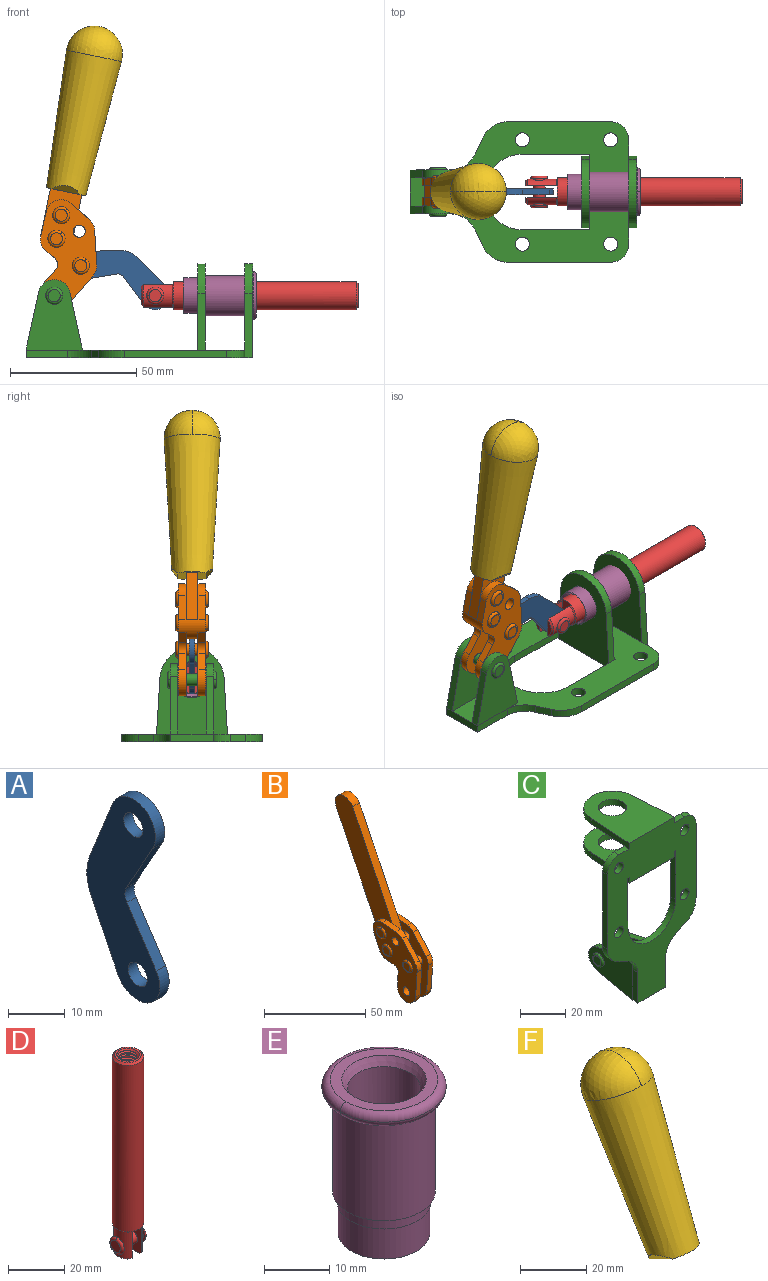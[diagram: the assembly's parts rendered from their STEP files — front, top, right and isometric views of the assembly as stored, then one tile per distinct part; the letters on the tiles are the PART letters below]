
ASSEMBLY  parts=6 mates=6
PART A: 12 faces, bbox 2.3x18.2x42.8 mm
  f0: cylinder r=2.4mm len=4.8mm, axis (1,0,0), area 34.9mm2, adj f4,f11
  f1: cylinder r=10.41mm len=8.47mm, axis (1,0,0), area 20.2mm2, adj f4,f9,f10,f11
  f2: cylinder r=3.05mm len=3.16mm, axis (1,0,0), area 7.7mm2, adj f4,f6,f7,f11
  f3: cylinder r=2.4mm len=4.8mm, axis (1,0,0), area 34.9mm2, adj f4,f11
  f4: plane 42.81x18.23mm, normal (-1,0,0), area 414.1mm2, adj f0,f1,f2,f3,f5,f6,f7,f8
  f5: cylinder r=5.54mm len=10.67mm, axis (1,0,0), area 41.8mm2, adj f4,f6,f10,f11
  f6: plane 11.66x6.53mm, normal (0,-0.87,-0.49), area 30.9mm2, adj f2,f4,f5,f11
  f7: plane 11.17x7.33mm, normal (0,-0.84,0.55), area 30.9mm2, adj f2,f4,f8,f11
  f8: cylinder r=5.54mm len=10.51mm, axis (1,0,0), area 41.8mm2, adj f4,f7,f9,f11
  f9: plane 13.67x6.67mm, normal (0,0.9,-0.44), area 35.1mm2, adj f1,f4,f8,f11
  f10: plane 14.1x5.7mm, normal (0,0.93,0.37), area 35.1mm2, adj f1,f4,f5,f11
  f11: plane 42.81x18.23mm, normal (1,0,0), area 414.1mm2, adj f0,f1,f2,f3,f5,f6,f7,f8
PART B: 59 faces, bbox 12.9x60.2x99.6 mm
  f0: torus R=2.39mm, axis (-1,0,0), area 14.9mm2, adj f20,f43,f51
  f1: torus R=2.39mm, axis (-1,0,0), area 14.9mm2, adj f19,f42,f51
  f2: torus R=2.39mm, axis (-1,0,0), area 14.9mm2, adj f18,f35,f51
  f3: torus R=2.39mm, axis (-1,0,0), area 14.9mm2, adj f14,f17,f23
  f4: torus R=2.39mm, axis (-1,0,0), area 14.9mm2, adj f13,f16,f23
  f5: torus R=2.39mm, axis (-1,0,0), area 14.9mm2, adj f12,f15,f23
  f6: cylinder r=2.39mm len=4.78mm, axis (1,0,0), area 46.5mm2, adj f48,f50,f51
  f7: cylinder r=2.39mm len=4.78mm, axis (1,0,0), area 46.5mm2, adj f50,f51
  f8: cylinder r=6.35mm len=12.68mm, axis (1,0,0), area 61.8mm2, adj f38,f39,f50,f51
  f9: cylinder r=2.39mm len=4.78mm, axis (-1,0,0), area 70.5mm2, adj f46,f50
  f10: cylinder r=2.39mm len=4.78mm, axis (-1,0,0), area 46.5mm2, adj f23,f45,f46
  f11: cylinder r=2.39mm len=4.78mm, axis (-1,0,0), area 46.5mm2, adj f23,f46
  f12: plane 4.78x4.78mm, normal (1,0,0), area 17.9mm2, adj f5,f15
  f13: plane 4.78x4.78mm, normal (1,0,0), area 17.9mm2, adj f4,f16
  f14: plane 4.78x4.78mm, normal (1,0,0), area 17.9mm2, adj f3,f17
  f15: torus R=2.39mm, axis (-1,0,0), area 14.9mm2, adj f5,f12,f23
  f16: torus R=2.39mm, axis (-1,0,0), area 14.9mm2, adj f4,f13,f23
  f17: torus R=2.39mm, axis (-1,0,0), area 14.9mm2, adj f3,f14,f23
  f18: plane 4.78x4.78mm, normal (-1,0,0), area 17.9mm2, adj f2,f35
  f19: plane 4.78x4.78mm, normal (-1,0,0), area 17.9mm2, adj f1,f42
  f20: plane 4.78x4.78mm, normal (-1,0,0), area 17.9mm2, adj f0,f43
  f21: plane 2.26x0.2mm, normal (1,0,0), area 0.2mm2, adj f31,f44
  f22: plane 2.26x0.2mm, normal (-1,0,0), area 0.2mm2, adj f41,f44
  f23: plane 39.37x30.77mm, normal (1,0,0), area 565.5mm2, adj f3,f4,f5,f10,f11,f15,f16,f17
  f24: cylinder r=6.1mm len=4.15mm, axis (-1,0,0), area 14.7mm2, adj f23,f25,f32,f46
  f25: plane 10.25x9.01mm, normal (0,-0.75,0.66), area 42.3mm2, adj f23,f24,f26,f46
  f26: cylinder r=6.35mm len=4.64mm, axis (-1,0,0), area 15.6mm2, adj f23,f25,f27,f46
  f27: plane 15.84x3.1mm, normal (0,-1,-0.07), area 49.2mm2, adj f23,f26,f28,f46
  f28: cylinder r=6.35mm len=12.68mm, axis (-1,0,0), area 61.8mm2, adj f23,f27,f29,f46
  f29: plane 8.11x3.1mm, normal (0,1,0.07), area 25.2mm2, adj f23,f28,f30,f46
  f30: cylinder r=3.05mm len=3.25mm, axis (-1,0,0), area 14.8mm2, adj f23,f29,f31,f46
  f31: plane 5.99x3.1mm, normal (0,0.07,-1), area 18.6mm2, adj f21,f23,f30,f44,f46
  f32: plane 9.5x3.1mm, normal (0,-0.07,1), area 29.5mm2, adj f23,f24,f33,f46,f47
  f33: cylinder r=6.1mm len=8.63mm, axis (-1,0,0), area 39.1mm2, adj f23,f32,f34,f47
  f34: plane 8.65x3.96mm, normal (0,0.91,-0.42), area 29.5mm2, adj f23,f33,f44,f47
  f35: torus R=2.39mm, axis (-1,0,0), area 14.9mm2, adj f2,f18,f51
  f36: plane 10.25x9.01mm, normal (0,-0.75,0.66), area 42.3mm2, adj f37,f49,f50,f51
  f37: cylinder r=6.35mm len=4.64mm, axis (1,0,0), area 15.6mm2, adj f36,f38,f50,f51
  f38: plane 15.84x3.1mm, normal (0,-1,-0.07), area 49.2mm2, adj f8,f37,f50,f51
  f39: plane 8.11x3.1mm, normal (0,1,0.07), area 25.2mm2, adj f8,f40,f50,f51
  f40: cylinder r=3.05mm len=3.25mm, axis (1,0,0), area 14.8mm2, adj f39,f41,f50,f51
  f41: plane 5.99x3.1mm, normal (0,0.07,-1), area 18.6mm2, adj f22,f40,f44,f50,f51
  f42: torus R=2.39mm, axis (-1,0,0), area 14.9mm2, adj f1,f19,f51
  f43: torus R=2.39mm, axis (-1,0,0), area 14.9mm2, adj f0,f20,f51
  f44: cylinder r=6.35mm len=12.12mm, axis (-1,0,0), area 128.9mm2, adj f21,f22,f23,f31,f34,f41,f46,f47
  f45: plane 2.65x1.35mm, normal (1,0,0), area 1mm2, adj f10,f55
  f46: plane 39.08x20.42mm, normal (-1,0,0), area 412.5mm2, adj f9,f10,f11,f24,f25,f26,f27,f28
  f47: plane 77.62x39.82mm, normal (1,0,0), area 850mm2, adj f32,f33,f34,f44,f53,f54,f55
  f48: plane 2.65x1.35mm, normal (-1,0,0), area 1mm2, adj f6,f55
  f49: cylinder r=6.1mm len=4.15mm, axis (1,0,0), area 14.7mm2, adj f36,f50,f51,f56
  f50: plane 39.08x20.42mm, normal (1,0,0), area 412.5mm2, adj f6,f7,f8,f9,f36,f37,f38,f39
  f51: plane 39.37x30.77mm, normal (-1,0,0), area 565.5mm2, adj f0,f1,f2,f6,f7,f8,f35,f36
  f52: plane 8.65x3.96mm, normal (0,0.91,-0.42), area 29.5mm2, adj f44,f51,f57,f58
  f53: plane 68.49x33.4mm, normal (0,0.9,-0.44), area 358.1mm2, adj f44,f47,f54,f58
  f54: cylinder r=6.35mm len=12.06mm, axis (1,0,0), area 93.7mm2, adj f47,f53,f55,f58
  f55: plane 68.49x33.4mm, normal (0,-0.9,0.44), area 358.1mm2, adj f44,f45,f46,f47,f48,f50,f54,f58
  f56: plane 9.5x3.1mm, normal (0,-0.07,1), area 29.5mm2, adj f49,f50,f51,f57,f58
  f57: cylinder r=6.1mm len=8.63mm, axis (1,0,0), area 39.1mm2, adj f51,f52,f56,f58
  f58: plane 77.62x39.82mm, normal (-1,0,0), area 850mm2, adj f44,f52,f53,f54,f55,f56,f57
PART C: 55 faces, bbox 55.7x37.4x89.8 mm
  f0: torus R=2.41mm, axis (-1,0,0), area 15mm2, adj f11,f15,f25
  f1: torus R=2.41mm, axis (-1,0,0), area 15mm2, adj f10,f12,f22
  f2: cylinder r=2.78mm len=5.56mm, axis (0,-1,0), area 54.2mm2, adj f30,f54
  f3: cylinder r=14.99mm len=29.97mm, axis (0,-1,0), area 145.9mm2, adj f30,f49,f53,f54
  f4: cylinder r=2.78mm len=5.56mm, axis (0,-1,0), area 54.2mm2, adj f30,f54
  f5: cylinder r=2.78mm len=5.56mm, axis (0,-1,0), area 54.2mm2, adj f30,f54
  f6: cylinder r=2.78mm len=5.56mm, axis (0,-1,0), area 54.2mm2, adj f30,f54
  f7: cylinder r=6.35mm len=12.7mm, axis (0,0,1), area 123.6mm2, adj f27,f51
  f8: cylinder r=6.35mm len=12.7mm, axis (0,0,-1), area 124.7mm2, adj f21,f35
  f9: cylinder r=2.41mm len=11.18mm, axis (-1,0,0), area 169.4mm2, adj f16,f19
  f10: plane 4.83x4.83mm, normal (1,0,0), area 18.3mm2, adj f1,f12
  f11: plane 4.83x4.83mm, normal (-1,0,0), area 18.3mm2, adj f0,f15
  f12: torus R=2.41mm, axis (-1,0,0), area 15mm2, adj f1,f10,f22
  f13: cylinder r=6.35mm len=12.41mm, axis (1,0,0), area 53.4mm2, adj f18,f19,f22,f23
  f14: cylinder r=6.35mm len=12.41mm, axis (-1,0,0), area 53.4mm2, adj f16,f17,f24,f25
  f15: torus R=2.41mm, axis (-1,0,0), area 15mm2, adj f0,f11,f25
  f16: plane 27.86x22.35mm, normal (1,0,0), area 425.4mm2, adj f9,f14,f17,f24,f30
  f17: plane 22.86x4.97mm, normal (0,0.21,0.98), area 72.5mm2, adj f14,f16,f25,f30
  f18: plane 22.86x4.97mm, normal (0,0.21,0.98), area 72.5mm2, adj f13,f19,f22,f30
  f19: plane 27.86x22.35mm, normal (-1,0,0), area 425.4mm2, adj f9,f13,f18,f23,f30
  f20: cylinder r=12.7mm len=25.35mm, axis (0,0,-1), area 119.8mm2, adj f21,f34,f35,f36
  f21: plane 34.21x28.07mm, normal (0,0,-1), area 702.4mm2, adj f8,f20,f30,f34,f36
  f22: plane 27.96x22.45mm, normal (1,0,0), area 407.2mm2, adj f1,f12,f13,f18,f23,f30,f42,f43
  f23: plane 22.86x4.97mm, normal (0,0.21,-0.98), area 72.5mm2, adj f13,f19,f22,f44
  f24: plane 22.86x4.97mm, normal (0,0.21,-0.98), area 72.5mm2, adj f14,f16,f25,f44
  f25: plane 27.86x22.35mm, normal (-1,0,0), area 407.1mm2, adj f0,f14,f15,f17,f24,f30,f45,f46
  f26: plane 3.1x0.95mm, normal (0,0,-1), area 2.7mm2, adj f30,f49,f50,f54
  f27: plane 34.21x28.07mm, normal (0,0,1), area 702.4mm2, adj f7,f28,f30,f50,f52
  f28: cylinder r=12.7mm len=25.35mm, axis (0,0,1), area 118.8mm2, adj f27,f50,f51,f52
  f29: plane 3.1x0.95mm, normal (0,0,-1), area 2.7mm2, adj f30,f52,f53,f54
  f30: plane 86.54x55.63mm, normal (0,1,0), area 2362.9mm2, adj f2,f3,f4,f5,f6,f16,f17,f18
  f31: plane 40.56x3.1mm, normal (-1,0,0), area 125.7mm2, adj f30,f32,f48,f54
  f32: cylinder r=7.11mm len=7.11mm, axis (0,-1,0), area 34.6mm2, adj f30,f31,f33,f54
  f33: plane 6.67x3.1mm, normal (0,0,1), area 20.4mm2, adj f30,f32,f34,f54
  f34: plane 25.39x3.13mm, normal (-1,0.06,0), area 79.5mm2, adj f20,f21,f33,f35,f54
  f35: plane 37.31x28.45mm, normal (0,0,1), area 789.9mm2, adj f8,f20,f34,f36,f54
  f36: plane 25.39x3.13mm, normal (1,0.06,0), area 79.5mm2, adj f20,f21,f35,f37,f54
  f37: plane 6.67x3.1mm, normal (0,0,1), area 20.4mm2, adj f30,f36,f38,f54
  f38: cylinder r=7.11mm len=7.11mm, axis (0,-1,0), area 34.6mm2, adj f30,f37,f39,f54
  f39: plane 40.56x3.1mm, normal (1,0,0), area 125.7mm2, adj f30,f38,f40,f54
  f40: cylinder r=11.18mm len=10.16mm, axis (0,-1,0), area 39.5mm2, adj f30,f39,f41,f54
  f41: plane 6.09x3.1mm, normal (0.42,0,-0.91), area 20.8mm2, adj f30,f40,f42,f54
  f42: cylinder r=11.18mm len=9.41mm, axis (0,-1,0), area 37.2mm2, adj f22,f30,f41,f43,f54
  f43: plane 16.5x3.1mm, normal (1,0,0), area 51.1mm2, adj f22,f42,f44,f54
  f44: plane 17.37x3.1mm, normal (0,0,-1), area 53.8mm2, adj f23,f24,f30,f43,f45,f54
  f45: plane 16.5x3.1mm, normal (-1,0,0), area 51.1mm2, adj f25,f44,f46,f54
  f46: cylinder r=11.18mm len=9.41mm, axis (0,-1,0), area 37.2mm2, adj f25,f30,f45,f47,f54
  f47: plane 6.09x3.1mm, normal (-0.42,0,-0.91), area 20.8mm2, adj f30,f46,f48,f54
  f48: cylinder r=11.18mm len=10.16mm, axis (0,-1,0), area 39.5mm2, adj f30,f31,f47,f54
  f49: plane 26.54x3.1mm, normal (-1,0,0), area 82.3mm2, adj f3,f26,f30,f54
  f50: plane 25.39x3.1mm, normal (1,0.06,0), area 78.8mm2, adj f26,f27,f28,f51,f54
  f51: plane 37.31x28.45mm, normal (0,0,-1), area 789.9mm2, adj f7,f28,f50,f52,f54
  f52: plane 25.39x3.1mm, normal (-1,0.06,0), area 78.8mm2, adj f27,f28,f29,f51,f54
  f53: plane 26.54x3.1mm, normal (1,0,0), area 82.3mm2, adj f3,f29,f30,f54
  f54: plane 89.66x55.63mm, normal (0,-1,0), area 2678.5mm2, adj f2,f3,f4,f5,f6,f26,f29,f31
PART D: 48 faces, bbox 12.6x11.1x86.1 mm
  f0: torus R=2.41mm, axis (-1,0,0), area 15mm2, adj f30,f32,f34
  f1: torus R=2.41mm, axis (-1,0,0), area 15mm2, adj f29,f31,f33
  f2: cylinder r=5.54mm len=72.39mm, axis (0,0,1), area 2518.5mm2, adj f3,f4,f42,f43
  f3: cone r=5.54mm half-angle=45deg, axis (0,0,1), area 7.6mm2, adj f2,f5,f41
  f4: cone r=5.54mm half-angle=45deg, axis (0,0,-1), area 34.9mm2, adj f2,f39
  f5: cylinder r=5.08mm len=11.48mm, axis (0,0,1), area 108.3mm2, adj f3,f7,f8,f41
  f6: cylinder r=2.41mm len=4.83mm, axis (-1,0,0), area 71.2mm2, adj f40,f41
  f7: cylinder r=2.41mm len=4.83mm, axis (-1,0,0), area 7.6mm2, adj f5,f34
  f8: cone r=5.08mm half-angle=45deg, axis (0,0,1), area 10.6mm2, adj f5,f37,f41
  f9: cone r=3.98mm half-angle=45deg, axis (0,0,1), area 17.6mm2, adj f27,f39,f45,f46,f47
  f10: cylinder r=2.41mm len=4.83mm, axis (-1,0,0), area 7.6mm2, adj f33,f38
  f11: cylinder r=3.2mm len=6.4mm, axis (0,0,1), area 78.4mm2, adj f12,f28,f44,f45,f47
  f12: cylinder r=3.2mm len=6.4mm, axis (0,0,1), area 10.5mm2, adj f11,f13,f45,f47
  f13: cylinder r=3.2mm len=6.4mm, axis (0,0,1), area 10.5mm2, adj f12,f14,f45,f47
  f14: cylinder r=3.2mm len=6.4mm, axis (0,0,1), area 10.5mm2, adj f13,f15,f45,f47
  f15: cylinder r=3.2mm len=6.4mm, axis (0,0,1), area 10.5mm2, adj f14,f16,f45,f47
  f16: cylinder r=3.2mm len=6.4mm, axis (0,0,1), area 10.5mm2, adj f15,f17,f45,f47
  f17: cylinder r=3.2mm len=6.4mm, axis (0,0,1), area 10.5mm2, adj f16,f18,f45,f47
  f18: cylinder r=3.2mm len=6.4mm, axis (0,0,1), area 10.5mm2, adj f17,f19,f45,f47
  f19: cylinder r=3.2mm len=6.4mm, axis (0,0,1), area 10.5mm2, adj f18,f20,f45,f47
  f20: cylinder r=3.2mm len=6.4mm, axis (0,0,1), area 10.5mm2, adj f19,f21,f45,f47
  f21: cylinder r=3.2mm len=6.4mm, axis (0,0,1), area 10.5mm2, adj f20,f22,f45,f47
  f22: cylinder r=3.2mm len=6.4mm, axis (0,0,1), area 10.5mm2, adj f21,f23,f45,f47
  f23: cylinder r=3.2mm len=6.4mm, axis (0,0,1), area 10.5mm2, adj f22,f24,f45,f47
  f24: cylinder r=3.2mm len=6.4mm, axis (0,0,1), area 10.5mm2, adj f23,f25,f45,f47
  f25: cylinder r=3.2mm len=6.4mm, axis (0,0,1), area 10.5mm2, adj f24,f26,f45,f47
  f26: cylinder r=3.2mm len=6.4mm, axis (0,0,1), area 10.5mm2, adj f25,f27,f45,f47
  f27: cylinder r=3.2mm len=6.4mm, axis (0,0,1), area 7.4mm2, adj f9,f26,f45,f47
  f28: cone r=3.2mm half-angle=60deg, axis (0,0,1), area 37.2mm2, adj f11
  f29: plane 4.83x4.83mm, normal (-1,0,0), area 18.3mm2, adj f1,f31
  f30: plane 4.83x4.83mm, normal (1,0,0), area 18.3mm2, adj f0,f32
  f31: torus R=2.41mm, axis (-1,0,0), area 15mm2, adj f1,f29,f33
  f32: torus R=2.41mm, axis (-1,0,0), area 15mm2, adj f0,f30,f34
  f33: plane 6.83x6.83mm, normal (1,0,0), area 18.3mm2, adj f1,f10,f31
  f34: plane 6.83x6.83mm, normal (-1,0,0), area 18.3mm2, adj f0,f7,f32
  f35: cone r=5.08mm half-angle=45deg, axis (0,0,1), area 10.6mm2, adj f36,f38,f40
  f36: plane 7.25x1.97mm, normal (0,0,-1), area 10mm2, adj f35,f40
  f37: plane 7.25x1.97mm, normal (0,0,-1), area 10mm2, adj f8,f41
  f38: cylinder r=5.08mm len=11.48mm, axis (0,0,1), area 108.3mm2, adj f10,f35,f40,f42
  f39: plane 9.55x9.55mm, normal (0,0,1), area 22mm2, adj f4,f9
  f40: plane 12.76x10.09mm, normal (1,0,0), area 95.7mm2, adj f6,f35,f36,f38,f42,f43
  f41: plane 12.76x10.09mm, normal (-1,0,0), area 95.7mm2, adj f3,f5,f6,f8,f37,f43
  f42: cone r=5.54mm half-angle=45deg, axis (0,0,1), area 7.6mm2, adj f2,f38,f40
  f43: plane 11.07x4.7mm, normal (0,0,-1), area 50.4mm2, adj f2,f40,f41
  f44: plane 0.89x0.62mm, normal (-1,0,0), area 0.3mm2, adj f11,f45,f46,f47
  f45: bspline ~24.8x7.63mm, area 266.6mm2, adj f9,f11,f12,f13,f14,f15,f16,f17
  f46: bspline ~24.87x7.63mm, area 73.6mm2, adj f9,f44,f45,f47
  f47: bspline ~24.98x7.63mm, area 272.5mm2, adj f9,f11,f12,f13,f14,f15,f16,f17
PART E: 15 faces, bbox 20.6x20.6x28.7 mm
  f0: torus R=8.26mm, axis (0,0,1), area 56.8mm2, adj f1,f10,f12
  f1: torus R=8.26mm, axis (0,0,1), area 56.8mm2, adj f0,f6,f13
  f2: cylinder r=5.59mm len=25.91mm, axis (0,0,1), area 909.6mm2, adj f3,f4
  f3: cone r=6.86mm half-angle=45deg, axis (0,0,-1), area 70.2mm2, adj f2,f14
  f4: cone r=6.47mm half-angle=30deg, axis (0,0,1), area 66.7mm2, adj f2,f13
  f5: cylinder r=7.04mm len=14.07mm, axis (0,0,1), area 252.6mm2, adj f11,f14
  f6: torus R=8.26mm, axis (0,0,1), area 56.8mm2, adj f1,f12,f13
  f7: cylinder r=7.16mm len=14.33mm, axis (0,0,1), area 91.5mm2, adj f9,f11
  f8: cylinder r=7.86mm len=18.42mm, axis (0,0,1), area 909.6mm2, adj f9,f10
  f9: plane 15.72x15.72mm, normal (0,0,-1), area 33mm2, adj f7,f8
  f10: plane 16.51x16.51mm, normal (0,0,-1), area 19.9mm2, adj f0,f8,f12
  f11: plane 14.33x14.33mm, normal (0,0,-1), area 5.7mm2, adj f5,f7
  f12: torus R=8.26mm, axis (0,0,1), area 56.8mm2, adj f0,f6,f10
  f13: plane 16.51x16.51mm, normal (0,0,1), area 82.7mm2, adj f1,f4,f6
  f14: plane 14.07x14.07mm, normal (0,0,-1), area 7.8mm2, adj f3,f5
PART F: 11 faces, bbox 22.3x42.6x64.5 mm
  f0: sphere r=11.13mm, area 411.4mm2, adj f1,f8
  f1: cone r=11.11mm half-angle=3.3deg, axis (0,0.44,0.9), area 3251.8mm2, adj f0,f7,f8,f9,f10
  f2: cylinder r=6.16mm len=11.7mm, axis (1,0,0), area 89.5mm2, adj f3,f4,f5,f6
  f3: plane 60.23x36.75mm, normal (-1,0,0), area 763.6mm2, adj f2,f4,f6,f10
  f4: plane 51.37x25.05mm, normal (0,0.9,-0.44), area 264.2mm2, adj f2,f3,f5,f10
  f5: plane 60.23x36.75mm, normal (1,0,0), area 763.6mm2, adj f2,f4,f6,f10
  f6: plane 51.37x25.05mm, normal (0,-0.9,0.44), area 264.2mm2, adj f2,f3,f5,f10
  f7: plane 9.95x5.95mm, normal (0.71,-0.31,-0.64), area 25.8mm2, adj f1,f10
  f8: sphere r=11.13mm, area 411.4mm2, adj f0,f1
  f9: plane 9.95x5.95mm, normal (-0.71,-0.31,-0.64), area 25.8mm2, adj f1,f10
  f10: plane 14.27x11.38mm, normal (0,-0.44,-0.9), area 106.7mm2, adj f1,f3,f4,f5,f6,f7,f9
PLACE A rot(axis=(0.5,-0.5,-0.71),109.2deg) t=(-21.99,2.31,15.77)mm
PLACE B rot(axis=(0.31,0.31,0.9),96deg) t=(0.41,2.31,42.74)mm
PLACE C rot(axis=(0.58,0.58,0.58),120deg) t=(-6.57,2.31,7.7)mm fixed
PLACE D rot(axis=(0.58,0.58,0.58),120deg) t=(-14.16,2.31,7.7)mm
PLACE E rot(axis=(0.71,0,0.71),180deg) t=(-7.59,26.92,32.31)mm
PLACE F rot(axis=(0.31,0.31,0.9),96deg) t=(0.41,2.27,42.74)mm
MATE slider D.f2 <-> E.f2  axis (1,0,0) through (44.62,2.31,32.31)mm
MATE revolute A.f5 <-> B.f4  axis (0,-1,0) through (-28.13,2.31,44.19)mm
MATE revolute A.f3 <-> D.f6  axis (0,-1,0) through (1.31,2.31,32.31)mm
MATE fastened C.f7 <-> E.f2  axis (1,0,0) through (39.82,2.31,32.31)mm
MATE revolute C.f0 <-> B.f7  axis (0,-1,0) through (-38.67,2.31,32.31)mm
MATE fastened F.f2 <-> B.f54  axis (0,1,0) through (-22.49,-0.04,129.47)mm
